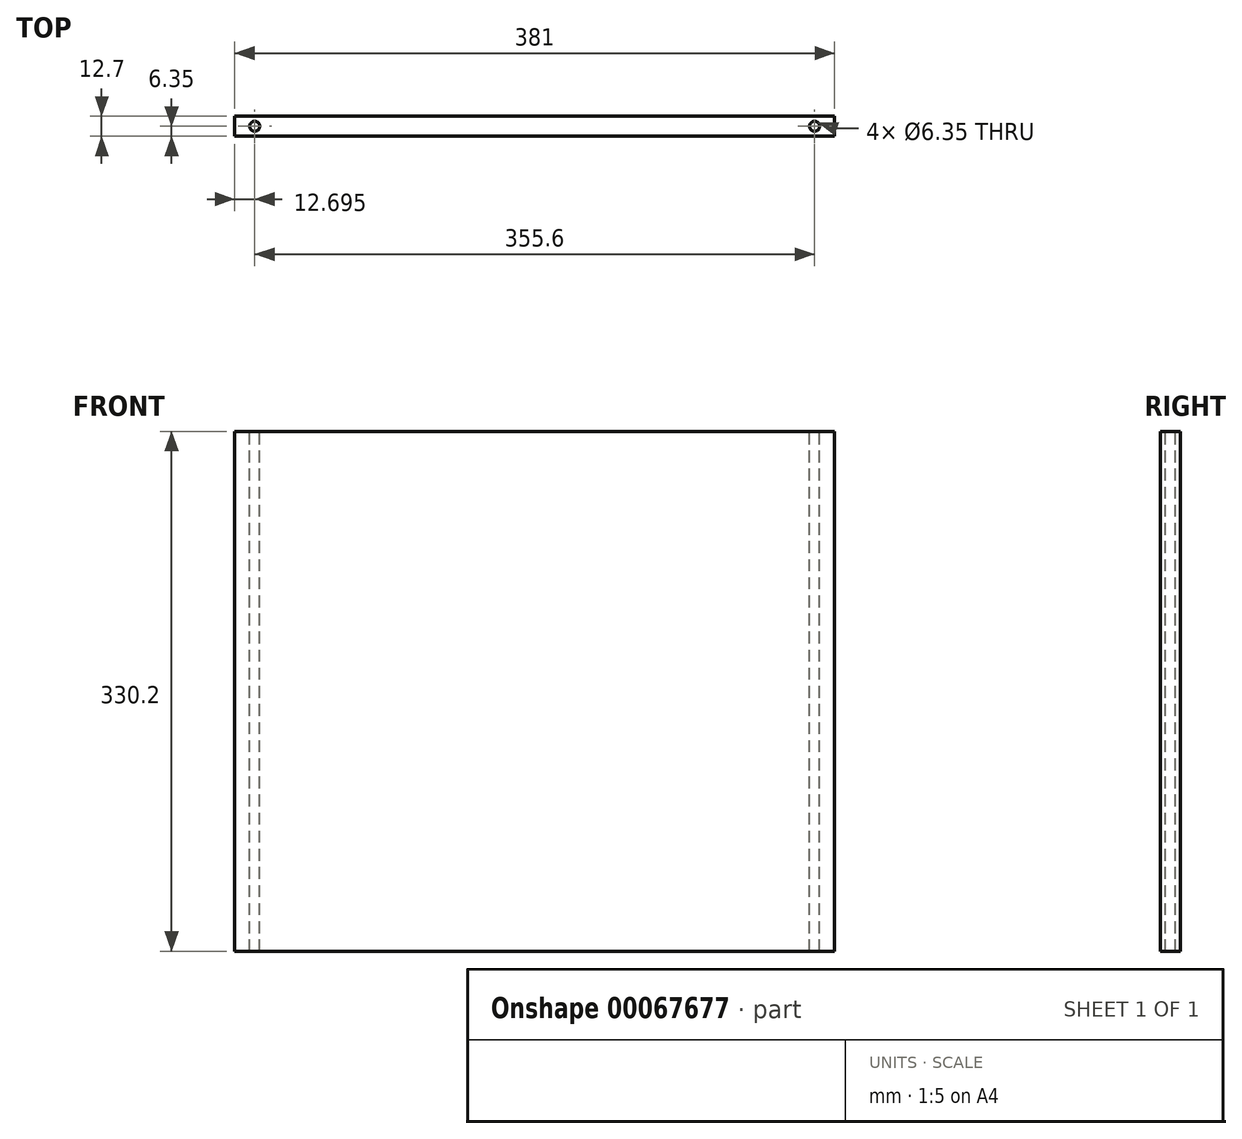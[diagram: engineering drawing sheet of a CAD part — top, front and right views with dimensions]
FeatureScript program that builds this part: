
annotation { "Feature Type Name" : "Feature", "Feature Type Description" : "" }
export const myFeature = defineFeature(function(context is Context, id is Id, definition is map)
    precondition{}
    {
        {
            var Q0;
            Q0=qCreatedBy(makeId("Front.planeOp"),FACE);
            var sketch = newSketch(context, id + "F0", { "sketchPlane" : qUnion([Q0])});
            skLineSegment(sketch, "E0.bottom", {"start": v(-163.17, 171.23) * mm, "end": v(217.83, 171.23) * mm});
            skLineSegment(sketch, "E0.top", {"start": v(-163.17, -158.97) * mm, "end": v(217.83, -158.97) * mm});
            skLineSegment(sketch, "E0.left", {"start": v(-163.17, 171.23) * mm, "end": v(-163.17, -158.97) * mm});
            skLineSegment(sketch, "E0.right", {"start": v(217.83, 171.23) * mm, "end": v(217.83, -158.97) * mm});
            skSolve(sketch);
        }
        {
            var Q0;
            Q0=makeQuery(id+"F0.imprint","IMPRINT",FACE,{"disambiguationData":[TD([[makeQuery(id+"F0.imprint","IMPRINT",EDGE,{"derivedFrom":sQuery(id+"F0.wireOp",EDGE,"E0.bottom")}),-1.0]])]});
            extrude(context, id + "F1", {"entities" : qUnion([Q0]), "depth" : 12.7 * mm});
        }
        {
            var Q0;
            Q0=makeQuery(id+"F1.opExtrude","SWEPT_FACE",FACE,{"disambiguationData":[OSD([sQuery(id+"F0.wireOp",EDGE,"E0.bottom")])]});
            var sketch = newSketch(context, id + "F2", { "sketchPlane" : qUnion([Q0])});
            skPoint(sketch, "E1", {"position": v(205.13, -6.35) * mm});
            skPoint(sketch, "E2", {"position": v(-150.47, -6.35) * mm});
            skSolve(sketch);
        }
        {
            var Q0;
            Q0=sQuery(id+"F2.wireOp",VERTEX,"E2");
            var Q1;
            Q1=sQuery(id+"F2.wireOp",VERTEX,"E1");
            var Q2;
            Q2=makeQuery(id+"F1.opExtrude","SWEPT_BODY",BODY,{"disambiguationData":[OSD([sQuery(id+"F0.wireOp",EDGE,"E0.bottom"),sQuery(id+"F0.wireOp",EDGE,"E0.top"),sQuery(id+"F0.wireOp",EDGE,"E0.left"),sQuery(id+"F0.wireOp",EDGE,"E0.right")])]});
            hole(context, id + "F3", {"style" : HoleStyle.SIMPLE, "holeDiameter" : 6.35 * mm, "endStyle" : HoleEndStyle.THROUGH, "locations" : qUnion([Q0, Q1]), "scope" : qUnion([Q2])});
        }
    });
